# Revit family: Water_Heater-Weil-McLain-Aqua_Plus
name_source: partatom
category: Mechanical Equipment
revit_build: Autodesk Revit MEP 2012 (Build: 20110916_2132(x64)
units: mm (PartAtom-declared; Revit-internal decimal feet)

## types (5) — shared parameters
316L Welded Stainless Steel Tank = Metal- Weil-McLain - Neutral
Boiler Flow = 0 GPM
Boiler Water In = 1"
Boiler Water In Radius = 1"
Boiler Water Out = 1"
Boiler Water Out Radius = 1"
DHW In = 1"
DHW Out = 1"
Description = Indirect-Fired Water Heater
Drain Flow = 0 GPM
Logo = Plastic - Weil-McLain - White
Manufacturer = Weil-McLain
Model = Aqua Plus
Plastic Casing = Plastic - Weil-McLain - Black
Poly Resin Top and Bottom = Plastic - Weil-McLain Poly Resin - Black
Product Documentation Link = http://www.weil-mclain.com
Product Name = Water Heater
Product Page URL = http://www.weil-mclain.com
Recirculation = 1"
URL = http://www.weil-mclain.com
Water Flow = 0 GPM
Working Pressure Coil = 145.00 psi
Working Pressure Tank = 150.00 psi

## per-type parameters (varying)
| type | Boiler Side Storage | Boiler Water Inlet | Boiler Water Outlet | Cold Water Inlet | DHW In Radius | DHW Operating Temp | DHW Out Radius | DHW Side Storage | Diameter | Domestic Water Recirculation Inlet | Head Loss Boiler Side | Height | Hot Water Outlet | Radius | Recirculation Radius | Recommended Flow Rated | Shipping Weight |
| 35 | 1.6 gal | 2' - 0" | 0' - 7 7/8" | 0' - 7 3/8" | 0" | 160 °F | 0" | 2.0 gal | 1' - 9 7/8" | 1' - 5 5/8" | 2' - 0" | 3' - 0 3/8" | 2' - 4" | 0' - 10 15/16" | 0" | 8 GPM | 94.00 lb |
| 45 | 1.9 gal | 2' - 2" | 0' - 7 7/8" | 0' - 7 3/8" | 0" | 160 °F | 0" | 39.9 gal | 1' - 9 7/8" | 1' - 9 1/4" | 3' - 3 19/32" | 3' - 10 1/4" | 3' - 1 7/8" | 0' - 10 15/16" | 0" | 8 GPM | 111.00 lb |
| 55 | 2.2 gal | 2' - 5 7/8" | 0' - 7 7/8" | 0' - 7 3/8" | 0" | 160 °F | 0" | 53.1 gal | 1' - 9 7/8" | 2' - 4 1/8" | 1' - 7 3/16" | 5' - 0" | 4' - 3 3/8" | 0' - 10 15/16" | 0" | 8 GPM | 122.00 lb |
| 85 | 2.5 gal | 2' - 9 1/4" | 0' - 10 3/8" | 0' - 8 7/8" | 1" | 180 °F | 1" | 80.6 gal | 2' - 2" | 2' - 7 1/2" | 5' - 4 13/16" | 4' - 11 1/2" | 4' - 2 3/8" | 1' - 1" | 1" | 14 GPM | 223.00 lb |
| 105 | 0.0 gal | 3' - 5 3/8" | 1' - 2 1/4" | 0' - 9 7/8" | 1" | -460 °F | 1" | 29.6 gal | 2' - 6" | 2' - 5 5/8" | 7' - 1 3/16" | 4' - 11 3/4" | 4' - 0 5/8" | 1' - 3" | 1" | 14 GPM | 238.00 lb |

## geometry (parser evidence)
native form markers: Blend x5, Sweep x3
no freeform markers — native parametric forms only
